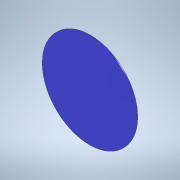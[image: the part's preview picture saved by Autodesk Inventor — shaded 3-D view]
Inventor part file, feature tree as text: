
AUTODESK INVENTOR PART (.ipt)
format: ipt  version: 2020.4 (Build 244396000, 396)  size: 95,232 bytes
history: native  units: mm
features: extrude x1, sketch x1
ambient origin geometry x8: Origin, YZ Plane, XZ Plane, XY Plane, X Axis, Y Axis, Z Axis, Center Point
bodies: Solid1 (feature_tree)
feature tree (2):
  extrude  "Extrusion1"  Depth=0.5mm TaperAngle=0.0deg
  sketch  "Sketch1"  dims[d0=52.0mm d1=0.5mm d2=0.0mm]
